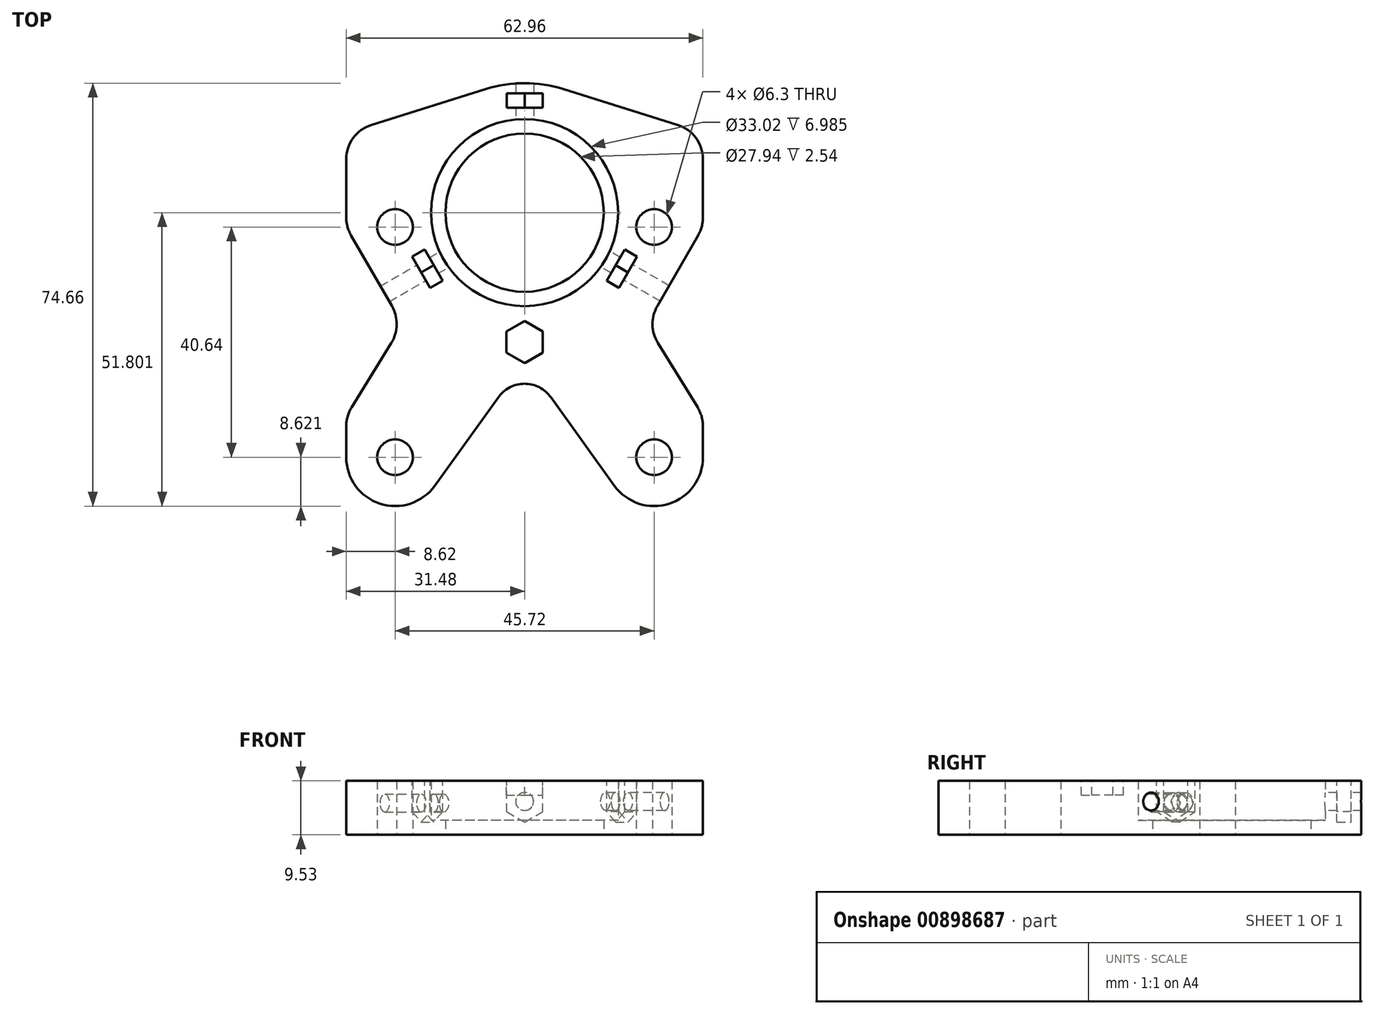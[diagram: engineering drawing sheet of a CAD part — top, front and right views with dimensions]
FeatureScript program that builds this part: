
annotation { "Feature Type Name" : "Feature", "Feature Type Description" : "" }
export const myFeature = defineFeature(function(context is Context, id is Id, definition is map)
    precondition{}
    {
        {
            var Q0;
            Q0=qCreatedBy(makeId("Top.planeOp"),FACE);
            var sketch = newSketch(context, id + "F0", { "sketchPlane" : qUnion([Q0])});
            skCircle(sketch, "E0", {"center": v(0, 35.92) * mm, "radius": 16.51 * mm});
            skCircle(sketch, "E1", {"center": v(-35.92, 35.92) * mm, "radius": 3.18 * mm, "construction": true});
            skCircle(sketch, "E2", {"center": v(35.92, 35.92) * mm, "radius": 3.18 * mm, "construction": true});
            skCircle(sketch, "E3", {"center": v(0, 0) * mm, "radius": 3.18 * mm, "construction": true});
            skLineSegment(sketch, "E4", {"start": v(32.75, 35.92) * mm, "end": v(32.75, -7.26) * mm, "construction": true});
            skCircle(sketch, "E5.0", {"center": v(0, 35.92) * mm, "radius": 13.97 * mm});
            skLineSegment(sketch, "E6", {"start": v(0, 35.92) * mm, "end": v(0, 52.43) * mm, "construction": true});
            skLineSegment(sketch, "E7", {"start": v(0, 35.92) * mm, "end": v(35.3, 15.54) * mm, "construction": true});
            skLineSegment(sketch, "E8", {"start": v(0, 35.92) * mm, "end": v(-35.36, 15.5) * mm, "construction": true});
            skCircle(sketch, "E9.cCircle", {"center": v(0, 35.92) * mm, "radius": 16.51 * mm, "construction": true});
            skLineSegment(sketch, "E9.0", {"start": v(9.53, 52.43) * mm, "end": v(19.06, 35.92) * mm, "construction": true});
            skLineSegment(sketch, "E9.1", {"start": v(19.06, 35.92) * mm, "end": v(9.53, 19.41) * mm, "construction": true});
            skLineSegment(sketch, "E9.2", {"start": v(9.53, 19.41) * mm, "end": v(-9.53, 19.41) * mm, "construction": true});
            skLineSegment(sketch, "E9.3", {"start": v(-9.53, 19.41) * mm, "end": v(-19.06, 35.92) * mm, "construction": true});
            skLineSegment(sketch, "E9.4", {"start": v(-19.06, 35.92) * mm, "end": v(-9.53, 52.43) * mm, "construction": true});
            skLineSegment(sketch, "E9.5", {"start": v(-9.53, 52.43) * mm, "end": v(9.53, 52.43) * mm, "construction": true});
            skPoint(sketch, "E9.0.midPoint", {"position": v(14.3, 44.18) * mm});
            skLineSegment(sketch, "E10", {"start": v(-35.92, 35.92) * mm, "end": v(35.92, 35.92) * mm, "construction": true});
            skCircle(sketch, "E11", {"center": v(-22.86, 33.38) * mm, "radius": 3.15 * mm});
            skCircle(sketch, "E12", {"center": v(22.86, 33.38) * mm, "radius": 3.15 * mm});
            skCircle(sketch, "E13", {"center": v(-22.86, -7.26) * mm, "radius": 3.15 * mm});
            skCircle(sketch, "E14", {"center": v(22.86, -7.26) * mm, "radius": 3.15 * mm});
            skLineSegment(sketch, "E15.bottom", {"start": v(-22.86, 33.38) * mm, "end": v(22.86, 33.38) * mm, "construction": true});
            skLineSegment(sketch, "E15.top", {"start": v(-22.86, -7.26) * mm, "end": v(22.86, -7.26) * mm, "construction": true});
            skLineSegment(sketch, "E15.left", {"start": v(-22.86, 33.38) * mm, "end": v(-22.86, -7.26) * mm, "construction": true});
            skLineSegment(sketch, "E15.right", {"start": v(22.86, 33.38) * mm, "end": v(22.86, -7.26) * mm, "construction": true});
            skLineSegment(sketch, "E16", {"start": v(-32.75, 35.92) * mm, "end": v(-32.75, -7.26) * mm, "construction": true});
            skLineSegment(sketch, "E17", {"start": v(-6.83, 57.74) * mm, "end": v(-27.02, 51.41) * mm});
            skLineSegment(sketch, "E18", {"start": v(-31.48, 45.35) * mm, "end": v(-31.48, 35.08) * mm});
            skLineSegment(sketch, "E19", {"start": v(6.83, 57.74) * mm, "end": v(27.02, 51.41) * mm});
            skLineSegment(sketch, "E20", {"start": v(31.48, 45.35) * mm, "end": v(31.48, 35.08) * mm});
            skArc(sketch, "E21.trimOffspring", {"start": v(6.83, 57.74) * mm, "mid": v(0, 58.78) * mm, "end": v(-6.83, 57.74) * mm});
            skArc(sketch, "E22.0", {"start": v(-31.48, -7.26) * mm, "mid": v(-25.5, -15.46) * mm, "end": v(-15.86, -12.29) * mm});
            skArc(sketch, "E23.0", {"start": v(15.86, -12.29) * mm, "mid": v(25.5, -15.46) * mm, "end": v(31.48, -7.26) * mm});
            skArc(sketch, "E24.0", {"start": v(4.64, 3.33) * mm, "mid": v(0, 5.72) * mm, "end": v(-4.64, 3.33) * mm});
            skLineSegment(sketch, "E25", {"start": v(-15.86, -12.29) * mm, "end": v(-4.64, 3.33) * mm});
            skLineSegment(sketch, "E26", {"start": v(4.64, 3.33) * mm, "end": v(15.86, -12.29) * mm});
            skLineSegment(sketch, "E27", {"start": v(-22.86, -7.26) * mm, "end": v(22.86, 33.38) * mm, "construction": true});
            skLineSegment(sketch, "E28", {"start": v(-22.86, 33.38) * mm, "end": v(22.86, -7.26) * mm, "construction": true});
            skPoint(sketch, "E29.visualSharp", {"position": v(-31.48, 50.02) * mm});
            skArc(sketch, "E29.filletArc", {"start": v(-27.02, 51.41) * mm, "mid": v(-30.24, 49.11) * mm, "end": v(-31.48, 45.35) * mm});
            skPoint(sketch, "E30.visualSharp", {"position": v(31.48, 50.02) * mm});
            skArc(sketch, "E30.filletArc", {"start": v(31.48, 45.35) * mm, "mid": v(30.24, 49.11) * mm, "end": v(27.02, 51.41) * mm});
            skLineSegment(sketch, "E31", {"start": v(30.63, 31.9) * mm, "end": v(23.43, 19.44) * mm});
            skLineSegment(sketch, "E32", {"start": v(23.52, 12.93) * mm, "end": v(30.53, 1.53) * mm});
            skLineSegment(sketch, "E33", {"start": v(-30.63, 31.9) * mm, "end": v(-23.43, 19.44) * mm});
            skLineSegment(sketch, "E34", {"start": v(-23.52, 12.93) * mm, "end": v(-30.53, 1.53) * mm});
            skLineSegment(sketch, "E35.trimOffspring", {"start": v(31.48, -1.8) * mm, "end": v(31.48, -7.26) * mm});
            skLineSegment(sketch, "E36.trimOffspring", {"start": v(-31.48, -1.8) * mm, "end": v(-31.48, -7.26) * mm});
            skPoint(sketch, "E37.visualSharp", {"position": v(-31.48, 33.38) * mm});
            skArc(sketch, "E37.filletArc", {"start": v(-31.48, 35.08) * mm, "mid": v(-31.26, 33.44) * mm, "end": v(-30.63, 31.9) * mm});
            skPoint(sketch, "E38.visualSharp", {"position": v(-21.53, 16.16) * mm});
            skArc(sketch, "E38.filletArc", {"start": v(-23.52, 12.93) * mm, "mid": v(-22.57, 16.17) * mm, "end": v(-23.43, 19.44) * mm});
            skPoint(sketch, "E39.visualSharp", {"position": v(-31.48, 0) * mm});
            skArc(sketch, "E39.filletArc", {"start": v(-30.53, 1.53) * mm, "mid": v(-31.24, -0.07) * mm, "end": v(-31.48, -1.8) * mm});
            skPoint(sketch, "E40.visualSharp", {"position": v(31.48, 33.38) * mm});
            skArc(sketch, "E40.filletArc", {"start": v(30.63, 31.9) * mm, "mid": v(31.26, 33.44) * mm, "end": v(31.48, 35.08) * mm});
            skPoint(sketch, "E41.visualSharp", {"position": v(21.53, 16.16) * mm});
            skArc(sketch, "E41.filletArc", {"start": v(23.43, 19.44) * mm, "mid": v(22.57, 16.17) * mm, "end": v(23.52, 12.93) * mm});
            skPoint(sketch, "E42.visualSharp", {"position": v(31.48, 0) * mm});
            skArc(sketch, "E42.filletArc", {"start": v(31.48, -1.8) * mm, "mid": v(31.24, -0.07) * mm, "end": v(30.53, 1.53) * mm});
            skSolve(sketch);
        }
        {
            var Q0;
            Q0=makeQuery(id+"F0.imprint","IMPRINT",FACE,{"disambiguationData":[TD([[makeQuery(id+"F0.imprint","IMPRINT",EDGE,{"derivedFrom":sQuery(id+"F0.wireOp",EDGE,"E0")}),-1.0]])]});
            extrude(context, id + "F1", {"entities" : qUnion([Q0]), "depth" : 9.52 * mm, "offsetDistance" : 25.4 * mm});
        }
        {
            var Q0;
            Q0=makeQuery(id+"F0.imprint","IMPRINT",FACE,{"disambiguationData":[TD([[makeQuery(id+"F0.imprint","IMPRINT",EDGE,{"derivedFrom":sQuery(id+"F0.wireOp",EDGE,"E0")}),1.0]])]});
            extrude(context, id + "F2", {"entities" : qUnion([Q0]), "operationType" : NewBodyOperationType.ADD, "depth" : 2.54 * mm, "hasOffset" : true, "offsetDistance" : 6.35 * mm});
        }
        {
            var Q0;
            Q0=makeQuery(id+"F1.opExtrude","CAP_FACE",FACE,{"disambiguationData":[OSD([sQuery(id+"F0.wireOp",EDGE,"EjYE8rPL-0voM-13ep-dpKR-Yhmu4oC0fMjX"),sQuery(id+"F0.wireOp",EDGE,"BDsdlpYl-4XZS-kb72-SQzJ-jy24um5DGsSm"),sQuery(id+"F0.wireOp",EDGE,"zDj9rnkT-zBYQ-YRrf-FuGE-prHvdQQL9E0l"),sQuery(id+"F0.wireOp",EDGE,"E0"),sQuery(id+"F0.wireOp",EDGE,"be656b23-60e4-4951-9072-4bb9fd2c1fe0.0"),sQuery(id+"F0.wireOp",EDGE,"adf94434-b9b2-4ff6-b419-fd79b20f5518.0"),sQuery(id+"F0.wireOp",EDGE,"4a9f2f50-e787-4006-96f4-ab8e54a99077.0"),sQuery(id+"F0.wireOp",EDGE,"02fbeba7-076e-4ed0-9f02-67362b93dccf.0"),sQuery(id+"F0.wireOp",EDGE,"R7reNZcb-uSRo-jru6-gR0G-eOQDTPOMIeGD"),sQuery(id+"F0.wireOp",EDGE,"i2Xnyxuy-PNx9-HtXw-tA11-sRRuayv3jRx9"),sQuery(id+"F0.wireOp",EDGE,"O9yRHGw0-B6N5-WUBC-CqYZ-9fVMz9zkHXct"),sQuery(id+"F0.wireOp",EDGE,"bXI39tXD-kIKO-QA8d-uo1d-AjNWw4kzWSzn"),sQuery(id+"F0.wireOp",EDGE,"yvXXFvSa-JQHm-aZvy-wO3q-0ffgoC5Wr51Q"),sQuery(id+"F0.wireOp",EDGE,"keBa6mA6-Ns36-as4S-D7yK-ubB9MYcM4YDE"),sQuery(id+"F0.wireOp",EDGE,"8eHimBAp-EooJ-JMgW-8GNK-FZK91k5yhUmU"),sQuery(id+"F0.wireOp",EDGE,"36RZBXD3-6qK0-qw5N-QxHJ-8RBiURi620yN"),sQuery(id+"F0.wireOp",EDGE,"1b80de2d-6fcf-4166-8bd7-bc7520118ab3.trimOffspring"),sQuery(id+"F0.wireOp",EDGE,"c2b8b45b-57a7-46a8-b7ff-993cbbd2993e.trimOffspring"),sQuery(id+"F0.wireOp",EDGE,"9e57da74-859c-4f91-937b-fdcaf8afdda5.filletArc"),sQuery(id+"F0.wireOp",EDGE,"2f08ad09-a47d-42bd-8f0e-b7f58f6490e4.filletArc"),sQuery(id+"F0.wireOp",EDGE,"30e6a12d-ff62-4460-809b-2951cf116d4f.filletArc"),sQuery(id+"F0.wireOp",EDGE,"3d167f00-72a4-4ff5-8a6d-0d591a0e7773.filletArc"),sQuery(id+"F0.wireOp",EDGE,"E4"),sQuery(id+"F0.wireOp",EDGE,"o9Ub0ZbI-FWSb-Ar0A-mzkB-0TMMgAmCBTNA"),sQuery(id+"F0.wireOp",EDGE,"02ed80ea-b338-46f1-988c-5186e078d909.trimOffspring"),sQuery(id+"F0.wireOp",EDGE,"bfc3d6b4-ed7b-404a-8939-94d15189dd00.filletArc"),sQuery(id+"F0.wireOp",EDGE,"d06de643-c4a7-4e1d-b592-4d839de3a7a0.filletArc")])],"isStart":false});
            var sketch = newSketch(context, id + "F3", { "sketchPlane" : qUnion([Q0])});
            skLineSegment(sketch, "E43", {"start": v(-3.18, 54.46) * mm, "end": v(-3.18, 57) * mm});
            skLineSegment(sketch, "E44", {"start": v(-3.18, 57) * mm, "end": v(3.17, 57) * mm});
            skLineSegment(sketch, "E45", {"start": v(3.17, 57) * mm, "end": v(3.17, 54.46) * mm});
            skLineSegment(sketch, "E46", {"start": v(3.17, 54.46) * mm, "end": v(-3.18, 54.46) * mm});
            skLineSegment(sketch, "E47", {"start": v(0, 52.43) * mm, "end": v(0, 54.46) * mm});
            skLineSegment(sketch, "E48.1.0", {"start": v(-17.65, 29.4) * mm, "end": v(-14.47, 23.9) * mm});
            skLineSegment(sketch, "E48.1.1", {"start": v(-19.85, 28.13) * mm, "end": v(-17.65, 29.4) * mm});
            skLineSegment(sketch, "E48.1.2", {"start": v(-16.67, 22.63) * mm, "end": v(-19.85, 28.13) * mm});
            skLineSegment(sketch, "E48.1.3", {"start": v(-14.47, 23.9) * mm, "end": v(-16.67, 22.63) * mm});
            skLineSegment(sketch, "E48.2.0", {"start": v(14.47, 23.9) * mm, "end": v(17.65, 29.4) * mm});
            skLineSegment(sketch, "E48.2.1", {"start": v(16.67, 22.63) * mm, "end": v(14.47, 23.9) * mm});
            skLineSegment(sketch, "E48.2.2", {"start": v(19.85, 28.13) * mm, "end": v(16.67, 22.63) * mm});
            skLineSegment(sketch, "E48.2.3", {"start": v(17.65, 29.4) * mm, "end": v(19.85, 28.13) * mm});
            skPoint(sketch, "E48.center", {"position": v(0, 35.92) * mm});
            skSolve(sketch);
        }
        {
            var Q0;
            Q0=makeQuery(id+"F3.imprint","IMPRINT",FACE,{"disambiguationData":[TD([[makeQuery(id+"F3.imprint","IMPRINT",EDGE,{"derivedFrom":sQuery(id+"F3.wireOp",EDGE,"E48.2.0")}),-1.0]])]});
            var Q1;
            {var subQ3=sQuery(id+"F3.wireOp",EDGE,"E43");Q1=makeQuery(id+"F3.imprint","IMPRINT",FACE,{"disambiguationData":[TD([[makeQuery(id+"F3.imprint","IMPRINT",EDGE,{"derivedFrom":subQ3}),-1.0]])]});}
            var Q2;
            Q2=makeQuery(id+"F3.imprint","IMPRINT",FACE,{"disambiguationData":[TD([[makeQuery(id+"F3.imprint","IMPRINT",EDGE,{"derivedFrom":sQuery(id+"F3.wireOp",EDGE,"E48.1.0")}),-1.0]])]});
            var Q3;
            {var subQ0=sQuery(id+"F3.wireOp",EDGE,"ymfYlLPS-t2fh-WVva-42DL-3NcaNd5SfhsS");Q3=makeQuery(id+"F3.imprint","IMPRINT",FACE,{"disambiguationData":[TD([[makeQuery(id+"F3.imprint","IMPRINT",EDGE,{"derivedFrom":subQ0}),-1.0]])]});}
            var Q4;
            {var subQ0=sQuery(id+"F3.wireOp",EDGE,"3a93bbba-05a9-4c98-87d1-4ddcdb9d8a6e");Q4=makeQuery(id+"F3.imprint","IMPRINT",FACE,{"disambiguationData":[TD([[makeQuery(id+"F3.imprint","IMPRINT",EDGE,{"derivedFrom":subQ0}),-1.0]])]});}
            var Q5;
            Q5=makeQuery(id+"F3.imprint","IMPRINT",FACE,{"disambiguationData":[TD([[makeQuery(id+"F3.imprint","IMPRINT",EDGE,{"derivedFrom":sQuery(id+"F3.wireOp",EDGE,"1bb13d12-811f-4404-9e1d-75ced0edb1cc")}),-1.0]])]});
            extrude(context, id + "F4", {"entities" : qUnion([Q0, Q1, Q2, Q3, Q4, Q5]), "operationType" : NewBodyOperationType.REMOVE, "oppositeDirection" : true, "depth" : 8.64 * mm, "offsetDistance" : 25.4 * mm});
        }
        {
            var Q0;
            Q0=makeQuery(id+"F4.boolean.opBoolean","COPY",EDGE,{"derivedFrom":makeQuery(id+"F4.opExtrude","CAP_EDGE",EDGE,{"disambiguationData":[OSD([sQuery(id+"F3.wireOp",EDGE,"E48.1.1")])],"isStart":false})});
            var Q1;
            Q1=makeQuery(id+"F4.boolean.opBoolean","COPY",EDGE,{"derivedFrom":makeQuery(id+"F4.opExtrude","CAP_EDGE",EDGE,{"disambiguationData":[OSD([sQuery(id+"F3.wireOp",EDGE,"E48.1.3")])],"isStart":false})});
            var Q2;
            Q2=makeQuery(id+"F4.boolean.opBoolean","COPY",EDGE,{"derivedFrom":makeQuery(id+"F4.opExtrude","CAP_EDGE",EDGE,{"disambiguationData":[OSD([sQuery(id+"F3.wireOp",EDGE,"E43")])],"isStart":false})});
            var Q3;
            Q3=makeQuery(id+"F4.boolean.opBoolean","COPY",EDGE,{"derivedFrom":makeQuery(id+"F4.opExtrude","CAP_EDGE",EDGE,{"disambiguationData":[OSD([sQuery(id+"F3.wireOp",EDGE,"E45")])],"isStart":false})});
            var Q4;
            Q4=makeQuery(id+"F4.boolean.opBoolean","COPY",EDGE,{"derivedFrom":makeQuery(id+"F4.opExtrude","CAP_EDGE",EDGE,{"disambiguationData":[OSD([sQuery(id+"F3.wireOp",EDGE,"E48.2.3")])],"isStart":false})});
            var Q5;
            Q5=makeQuery(id+"F4.boolean.opBoolean","COPY",EDGE,{"derivedFrom":makeQuery(id+"F4.opExtrude","CAP_EDGE",EDGE,{"disambiguationData":[OSD([sQuery(id+"F3.wireOp",EDGE,"E48.2.1")])],"isStart":false})});
            var Q6;
            Q6=makeQuery(id+"F4.boolean.opBoolean","COPY",EDGE,{"derivedFrom":makeQuery(id+"F4.opExtrude","CAP_EDGE",EDGE,{"disambiguationData":[OSD([sQuery(id+"F3.wireOp",EDGE,"EVzcqgKL-xezH-Hxx2-NkCw-EC7lOrHd5Xnc")])],"isStart":false})});
            var Q7;
            Q7=makeQuery(id+"F4.boolean.opBoolean","COPY",EDGE,{"derivedFrom":makeQuery(id+"F4.opExtrude","CAP_EDGE",EDGE,{"disambiguationData":[OSD([sQuery(id+"F3.wireOp",EDGE,"ymfYlLPS-t2fh-WVva-42DL-3NcaNd5SfhsS")])],"isStart":false})});
            var Q8;
            Q8=makeQuery(id+"F4.boolean.opBoolean","COPY",EDGE,{"derivedFrom":makeQuery(id+"F4.opExtrude","CAP_EDGE",EDGE,{"disambiguationData":[OSD([sQuery(id+"F3.wireOp",EDGE,"236dffc3-8eaa-4971-9524-ae12a32c2ead")])],"isStart":false})});
            var Q9;
            Q9=makeQuery(id+"F4.boolean.opBoolean","COPY",EDGE,{"derivedFrom":makeQuery(id+"F4.opExtrude","CAP_EDGE",EDGE,{"disambiguationData":[OSD([sQuery(id+"F3.wireOp",EDGE,"c035f3bf-e4a5-496b-bfbc-999cd9edc6f8")])],"isStart":false})});
            var Q10;
            Q10=makeQuery(id+"F4.boolean.opBoolean","COPY",EDGE,{"derivedFrom":makeQuery(id+"F4.opExtrude","CAP_EDGE",EDGE,{"disambiguationData":[OSD([sQuery(id+"F3.wireOp",EDGE,"3a93bbba-05a9-4c98-87d1-4ddcdb9d8a6e")])],"isStart":false})});
            var Q11;
            Q11=makeQuery(id+"F4.boolean.opBoolean","COPY",EDGE,{"derivedFrom":makeQuery(id+"F4.opExtrude","CAP_EDGE",EDGE,{"disambiguationData":[OSD([sQuery(id+"F3.wireOp",EDGE,"de81c6bc-ae6e-4456-97cb-3c9b7336e4ed")])],"isStart":false})});
            chamfer(context, id + "F5", {"entities" : qUnion([Q0, Q1, Q2, Q3, Q4, Q5, Q6, Q7, Q8, Q9, Q10, Q11]), "chamferType" : ChamferType.OFFSET_ANGLE, "width" : 3.17 * mm, "oppositeDirection" : false, "angle" : 60 * degree, "tangentPropagation" : true});
        }
        {
            var Q0;
            Q0=makeQuery(id+"F4.boolean.opBoolean","COPY",FACE,{"derivedFrom":makeQuery(id+"F4.opExtrude","SWEPT_FACE",FACE,{"disambiguationData":[OSD([sQuery(id+"F3.wireOp",EDGE,"E44")])]})});
            var sketch = newSketch(context, id + "F6", { "sketchPlane" : qUnion([Q0])});
            skLineSegment(sketch, "E49", {"start": v(3.18, 4.06) * mm, "end": v(0, 2.23) * mm});
            skLineSegment(sketch, "E50", {"start": v(0, 2.23) * mm, "end": v(-3.17, 4.06) * mm});
            skLineSegment(sketch, "E51", {"start": v(-3.17, 4.06) * mm, "end": v(-3.17, 7.73) * mm});
            skLineSegment(sketch, "E52", {"start": v(3.18, 7.73) * mm, "end": v(3.18, 4.06) * mm});
            skLineSegment(sketch, "E53", {"start": v(3.18, 7.73) * mm, "end": v(0, 9.56) * mm});
            skPoint(sketch, "E53.endSnap0", {"position": v(0, 9.53) * mm});
            skLineSegment(sketch, "E54", {"start": v(0, 9.56) * mm, "end": v(-3.18, 7.73) * mm});
            skLineSegment(sketch, "E55", {"start": v(0, 2.23) * mm, "end": v(0, 5.9) * mm, "construction": true});
            skLineSegment(sketch, "E56", {"start": v(0, 5.9) * mm, "end": v(-3.18, 4.06) * mm, "construction": true});
            skLineSegment(sketch, "E57", {"start": v(0, 5.9) * mm, "end": v(3.18, 7.73) * mm, "construction": true});
            skLineSegment(sketch, "E58", {"start": v(0, 5.9) * mm, "end": v(0, 9.56) * mm, "construction": true});
            skCircle(sketch, "E59", {"center": v(0, 5.9) * mm, "radius": 1.59 * mm});
            skSolve(sketch);
        }
        {
            var Q0;
            Q0=makeQuery(id+"F4.boolean.opBoolean","COPY",FACE,{"derivedFrom":makeQuery(id+"F4.opExtrude","SWEPT_FACE",FACE,{"disambiguationData":[OSD([sQuery(id+"F3.wireOp",EDGE,"E48.1.2")])]})});
            var sketch = newSketch(context, id + "F7", { "sketchPlane" : qUnion([Q0])});
            skLineSegment(sketch, "E60", {"start": v(34.2, 3.78) * mm, "end": v(31.03, 1.94) * mm});
            skLineSegment(sketch, "E61", {"start": v(31.03, 1.94) * mm, "end": v(27.86, 3.78) * mm});
            skLineSegment(sketch, "E62", {"start": v(27.86, 3.78) * mm, "end": v(27.86, 7.44) * mm});
            skLineSegment(sketch, "E63", {"start": v(34.2, 7.44) * mm, "end": v(34.2, 3.78) * mm});
            skLineSegment(sketch, "E64", {"start": v(34.2, 7.44) * mm, "end": v(31.03, 9.26) * mm});
            skLineSegment(sketch, "E65", {"start": v(31.03, 9.26) * mm, "end": v(27.86, 7.44) * mm});
            skCircle(sketch, "E66", {"center": v(31.03, 5.6) * mm, "radius": 1.59 * mm});
            skSolve(sketch);
        }
        {
            var Q0;
            Q0=makeQuery(id+"F4.boolean.opBoolean","COPY",FACE,{"derivedFrom":makeQuery(id+"F4.opExtrude","SWEPT_FACE",FACE,{"disambiguationData":[OSD([sQuery(id+"F3.wireOp",EDGE,"E48.2.2")])]})});
            var sketch = newSketch(context, id + "F8", { "sketchPlane" : qUnion([Q0])});
            skLineSegment(sketch, "E67", {"start": v(-27.95, 4.06) * mm, "end": v(-31.12, 2.24) * mm});
            skLineSegment(sketch, "E68", {"start": v(-31.12, 2.24) * mm, "end": v(-34.28, 4.06) * mm});
            skLineSegment(sketch, "E69", {"start": v(-34.28, 4.06) * mm, "end": v(-34.28, 7.72) * mm});
            skLineSegment(sketch, "E70", {"start": v(-27.95, 7.72) * mm, "end": v(-27.95, 4.06) * mm});
            skLineSegment(sketch, "E71", {"start": v(-27.95, 7.72) * mm, "end": v(-31.12, 9.55) * mm});
            skLineSegment(sketch, "E72", {"start": v(-31.12, 9.55) * mm, "end": v(-34.28, 7.72) * mm});
            skCircle(sketch, "E73", {"center": v(-31.12, 5.9) * mm, "radius": 1.59 * mm});
            skLineSegment(sketch, "E74", {"start": v(-31.12, 2.24) * mm, "end": v(-31.12, 5.9) * mm, "construction": true});
            skLineSegment(sketch, "E75", {"start": v(-31.12, 5.9) * mm, "end": v(-34.28, 4.06) * mm, "construction": true});
            skLineSegment(sketch, "E76", {"start": v(-31.12, 9.55) * mm, "end": v(-31.12, 5.9) * mm, "construction": true});
            skLineSegment(sketch, "E77", {"start": v(-27.95, 7.72) * mm, "end": v(-31.12, 5.9) * mm, "construction": true});
            skSolve(sketch);
        }
        {
            var Q0;
            Q0=makeQuery(id+"F6.imprint","IMPRINT",FACE,{"disambiguationData":[TD([[makeQuery(id+"F6.imprint","IMPRINT",EDGE,{"derivedFrom":sQuery(id+"F6.wireOp",EDGE,"E59")}),1.0]])]});
            extrude(context, id + "F9", {"entities" : qUnion([Q0]), "operationType" : NewBodyOperationType.REMOVE, "oppositeDirection" : true, "depth" : 10.16 * mm, "offsetDistance" : 25.4 * mm, "symmetric" : true});
        }
        {
            var Q0;
            Q0=makeQuery(id+"F7.imprint","IMPRINT",FACE,{"disambiguationData":[TD([[makeQuery(id+"F7.imprint","IMPRINT",EDGE,{"derivedFrom":sQuery(id+"F7.wireOp",EDGE,"E66")}),1.0]])]});
            var Q1;
            Q1=sQuery(id+"F7.wireOp",EDGE,"E66");
            extrude(context, id + "F10", {"entities" : qUnion([Q0]), "operationType" : NewBodyOperationType.REMOVE, "surfaceEntities" : qUnion([Q1]), "oppositeDirection" : true, "depth" : 40.64 * mm, "offsetDistance" : 25.4 * mm, "symmetric" : true});
        }
        {
            var Q0;
            Q0=makeQuery(id+"F8.imprint","IMPRINT",FACE,{"disambiguationData":[TD([[makeQuery(id+"F8.imprint","IMPRINT",EDGE,{"derivedFrom":sQuery(id+"F8.wireOp",EDGE,"E73")}),1.0]])]});
            var Q1;
            Q1=sQuery(id+"F8.wireOp",EDGE,"E73");
            extrude(context, id + "F11", {"entities" : qUnion([Q0]), "operationType" : NewBodyOperationType.REMOVE, "surfaceEntities" : qUnion([Q1]), "oppositeDirection" : true, "depth" : 40.64 * mm, "offsetDistance" : 25.4 * mm, "symmetric" : true});
        }
        {
            var Q0;
            Q0=makeQuery(id+"F1.opExtrude","CAP_FACE",FACE,{"disambiguationData":[OSD([sQuery(id+"F0.wireOp",EDGE,"E0"),sQuery(id+"F0.wireOp",EDGE,"E11"),sQuery(id+"F0.wireOp",EDGE,"E12"),sQuery(id+"F0.wireOp",EDGE,"E13"),sQuery(id+"F0.wireOp",EDGE,"E14"),sQuery(id+"F0.wireOp",EDGE,"E17"),sQuery(id+"F0.wireOp",EDGE,"E18"),sQuery(id+"F0.wireOp",EDGE,"E19"),sQuery(id+"F0.wireOp",EDGE,"E20"),sQuery(id+"F0.wireOp",EDGE,"E21.trimOffspring"),sQuery(id+"F0.wireOp",EDGE,"E22.0"),sQuery(id+"F0.wireOp",EDGE,"E23.0"),sQuery(id+"F0.wireOp",EDGE,"E24.0"),sQuery(id+"F0.wireOp",EDGE,"E25"),sQuery(id+"F0.wireOp",EDGE,"E26"),sQuery(id+"F0.wireOp",EDGE,"E29.filletArc"),sQuery(id+"F0.wireOp",EDGE,"E30.filletArc"),sQuery(id+"F0.wireOp",EDGE,"E31"),sQuery(id+"F0.wireOp",EDGE,"E32"),sQuery(id+"F0.wireOp",EDGE,"E33"),sQuery(id+"F0.wireOp",EDGE,"E34"),sQuery(id+"F0.wireOp",EDGE,"E35.trimOffspring"),sQuery(id+"F0.wireOp",EDGE,"E36.trimOffspring"),sQuery(id+"F0.wireOp",EDGE,"E37.filletArc"),sQuery(id+"F0.wireOp",EDGE,"E38.filletArc"),sQuery(id+"F0.wireOp",EDGE,"E39.filletArc"),sQuery(id+"F0.wireOp",EDGE,"E40.filletArc"),sQuery(id+"F0.wireOp",EDGE,"E41.filletArc"),sQuery(id+"F0.wireOp",EDGE,"E42.filletArc")])],"isStart":false});
            var sketch = newSketch(context, id + "F12", { "sketchPlane" : qUnion([Q0])});
            skLineSegment(sketch, "E78", {"start": v(-22.86, -7.26) * mm, "end": v(22.86, 33.38) * mm, "construction": true});
            skLineSegment(sketch, "E79", {"start": v(-22.86, 33.38) * mm, "end": v(22.86, -7.26) * mm, "construction": true});
            skCircle(sketch, "E80.cCircle", {"center": v(0, 13.06) * mm, "radius": 3.23 * mm, "construction": true});
            skLineSegment(sketch, "E80.0", {"start": v(3.23, 14.92) * mm, "end": v(3.23, 11.2) * mm});
            skLineSegment(sketch, "E80.1", {"start": v(3.23, 11.2) * mm, "end": v(0, 9.34) * mm});
            skLineSegment(sketch, "E80.2", {"start": v(0, 9.34) * mm, "end": v(-3.23, 11.2) * mm});
            skLineSegment(sketch, "E80.3", {"start": v(-3.23, 11.2) * mm, "end": v(-3.23, 14.92) * mm});
            skLineSegment(sketch, "E80.4", {"start": v(-3.23, 14.92) * mm, "end": v(0, 16.79) * mm});
            skLineSegment(sketch, "E80.5", {"start": v(0, 16.79) * mm, "end": v(3.23, 14.92) * mm});
            skPoint(sketch, "E80.0.midPoint", {"position": v(3.23, 13.06) * mm});
            skSolve(sketch);
        }
        {
            var Q0;
            Q0=makeQuery(id+"F12.imprint","IMPRINT",FACE,{"disambiguationData":[TD([[makeQuery(id+"F12.imprint","IMPRINT",EDGE,{"derivedFrom":sQuery(id+"F12.wireOp",EDGE,"E80.0")}),-1.0]])]});
            extrude(context, id + "F13", {"entities" : qUnion([Q0]), "operationType" : NewBodyOperationType.REMOVE, "oppositeDirection" : true, "depth" : 2.54 * mm, "offsetDistance" : 25.4 * mm});
        }
        {
            var Q0;
            Q0=makeQuery(id+"F1.opExtrude","SWEPT_BODY",BODY,{"disambiguationData":[OSD([sQuery(id+"F0.wireOp",EDGE,"E0"),sQuery(id+"F0.wireOp",EDGE,"E11"),sQuery(id+"F0.wireOp",EDGE,"E12"),sQuery(id+"F0.wireOp",EDGE,"E13"),sQuery(id+"F0.wireOp",EDGE,"E14"),sQuery(id+"F0.wireOp",EDGE,"E17"),sQuery(id+"F0.wireOp",EDGE,"E18"),sQuery(id+"F0.wireOp",EDGE,"E19"),sQuery(id+"F0.wireOp",EDGE,"E20"),sQuery(id+"F0.wireOp",EDGE,"E21.trimOffspring"),sQuery(id+"F0.wireOp",EDGE,"E22.0"),sQuery(id+"F0.wireOp",EDGE,"E23.0"),sQuery(id+"F0.wireOp",EDGE,"E24.0"),sQuery(id+"F0.wireOp",EDGE,"E25"),sQuery(id+"F0.wireOp",EDGE,"E26"),sQuery(id+"F0.wireOp",EDGE,"E29.filletArc"),sQuery(id+"F0.wireOp",EDGE,"E30.filletArc"),sQuery(id+"F0.wireOp",EDGE,"E31"),sQuery(id+"F0.wireOp",EDGE,"E32"),sQuery(id+"F0.wireOp",EDGE,"E33"),sQuery(id+"F0.wireOp",EDGE,"E34"),sQuery(id+"F0.wireOp",EDGE,"E35.trimOffspring"),sQuery(id+"F0.wireOp",EDGE,"E36.trimOffspring"),sQuery(id+"F0.wireOp",EDGE,"E37.filletArc"),sQuery(id+"F0.wireOp",EDGE,"E38.filletArc"),sQuery(id+"F0.wireOp",EDGE,"E39.filletArc"),sQuery(id+"F0.wireOp",EDGE,"E40.filletArc"),sQuery(id+"F0.wireOp",EDGE,"E41.filletArc"),sQuery(id+"F0.wireOp",EDGE,"E42.filletArc")])]});
            transform(context, id + "F14", {"entities" : qUnion([Q0]), "transformType" : TransformType.TRANSLATION_3D, "dx" : 0 * mm, "dy" : 0 * mm, "dz" : 0 * mm, "makeCopy" : true});
        }
        {
            var Q0;
            Q0=makeQuery(id+"F14.opPattern","COPY",BODY,{"derivedFrom":makeQuery(id+"F1.opExtrude","SWEPT_BODY",BODY,{"disambiguationData":[OSD([sQuery(id+"F0.wireOp",EDGE,"E0"),sQuery(id+"F0.wireOp",EDGE,"E11"),sQuery(id+"F0.wireOp",EDGE,"E12"),sQuery(id+"F0.wireOp",EDGE,"E13"),sQuery(id+"F0.wireOp",EDGE,"E14"),sQuery(id+"F0.wireOp",EDGE,"E17"),sQuery(id+"F0.wireOp",EDGE,"E18"),sQuery(id+"F0.wireOp",EDGE,"E19"),sQuery(id+"F0.wireOp",EDGE,"E20"),sQuery(id+"F0.wireOp",EDGE,"E21.trimOffspring"),sQuery(id+"F0.wireOp",EDGE,"E22.0"),sQuery(id+"F0.wireOp",EDGE,"E23.0"),sQuery(id+"F0.wireOp",EDGE,"E24.0"),sQuery(id+"F0.wireOp",EDGE,"E25"),sQuery(id+"F0.wireOp",EDGE,"E26"),sQuery(id+"F0.wireOp",EDGE,"E29.filletArc"),sQuery(id+"F0.wireOp",EDGE,"E30.filletArc"),sQuery(id+"F0.wireOp",EDGE,"E31"),sQuery(id+"F0.wireOp",EDGE,"E32"),sQuery(id+"F0.wireOp",EDGE,"E33"),sQuery(id+"F0.wireOp",EDGE,"E34"),sQuery(id+"F0.wireOp",EDGE,"E35.trimOffspring"),sQuery(id+"F0.wireOp",EDGE,"E36.trimOffspring"),sQuery(id+"F0.wireOp",EDGE,"E37.filletArc"),sQuery(id+"F0.wireOp",EDGE,"E38.filletArc"),sQuery(id+"F0.wireOp",EDGE,"E39.filletArc"),sQuery(id+"F0.wireOp",EDGE,"E40.filletArc"),sQuery(id+"F0.wireOp",EDGE,"E41.filletArc"),sQuery(id+"F0.wireOp",EDGE,"E42.filletArc")])]}),"instanceName":"1"});
            deleteBodies(context, id + "F15", {"entities" : qUnion([Q0])});
        }
    });
